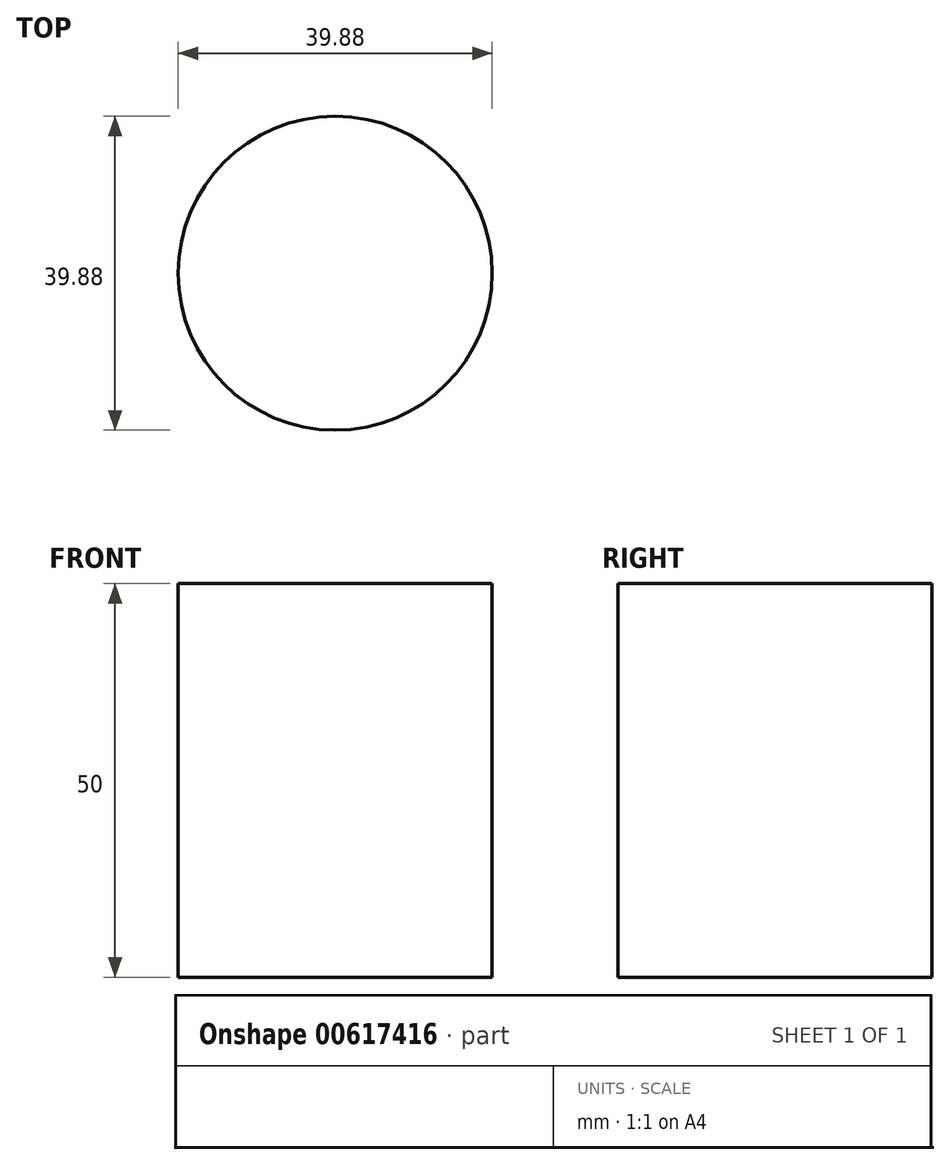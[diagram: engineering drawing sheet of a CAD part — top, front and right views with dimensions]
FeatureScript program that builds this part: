
annotation { "Feature Type Name" : "Feature", "Feature Type Description" : "" }
export const myFeature = defineFeature(function(context is Context, id is Id, definition is map)
    precondition{}
    {
        {
            var Q0;
            Q0=qCreatedBy(makeId("Top.planeOp"),FACE);
            var sketch = newSketch(context, id + "F0", { "sketchPlane" : qUnion([Q0])});
            skCircle(sketch, "E0", {"center": v(0, 0) * mm, "radius": 19.94 * mm});
            skSolve(sketch);
        }
        {
            var Q0;
            Q0=makeQuery(id+"F0.imprint","IMPRINT",FACE,{"disambiguationData":[TD([[makeQuery(id+"F0.imprint","IMPRINT",EDGE,{"derivedFrom":sQuery(id+"F0.wireOp",EDGE,"E0")}),1.0]])]});
            extrude(context, id + "F1", {"entities" : qUnion([Q0]), "depth" : 50 * mm, "offsetDistance" : 25 * mm});
        }
    });
